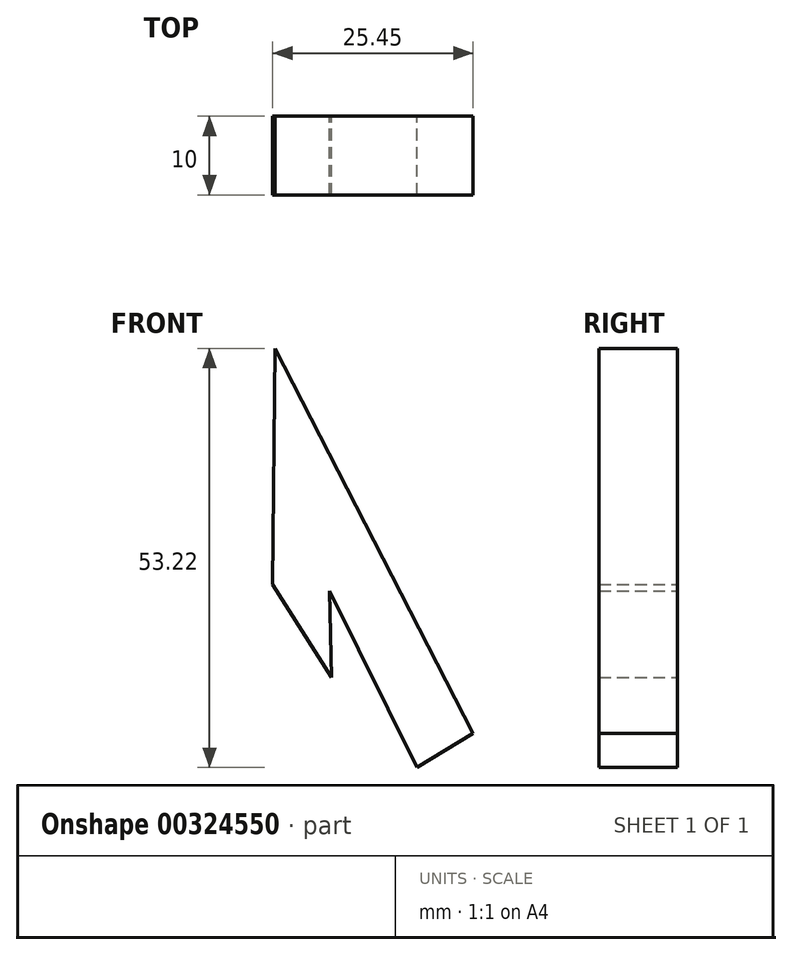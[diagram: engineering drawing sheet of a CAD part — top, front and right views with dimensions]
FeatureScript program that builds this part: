
annotation { "Feature Type Name" : "Feature", "Feature Type Description" : "" }
export const myFeature = defineFeature(function(context is Context, id is Id, definition is map)
    precondition{}
    {
        {
            var Q0;
            Q0=qCreatedBy(makeId("Front.planeOp"),FACE);
            var sketch = newSketch(context, id + "F0", { "sketchPlane" : qUnion([Q0])});
            skPoint(sketch, "E0", {"position": v(0, 0) * mm});
            skPoint(sketch, "E1", {"position": v(-25.12, 48.93) * mm});
            skLineSegment(sketch, "E2", {"start": v(-25.12, 48.93) * mm, "end": v(0, 0) * mm});
            skPoint(sketch, "E3", {"position": v(-25.45, 18.93) * mm});
            skLineSegment(sketch, "E4", {"start": v(-25.45, 18.93) * mm, "end": v(-25.12, 48.93) * mm});
            skPoint(sketch, "E5", {"position": v(-17.95, 7.1) * mm});
            skLineSegment(sketch, "E6", {"start": v(-17.95, 7.1) * mm, "end": v(-25.45, 18.93) * mm});
            skPoint(sketch, "E7", {"position": v(-18.21, 18.1) * mm});
            skLineSegment(sketch, "E8", {"start": v(-18.21, 18.1) * mm, "end": v(-17.95, 7.1) * mm});
            skPoint(sketch, "E9", {"position": v(-7.1, -4.3) * mm});
            skLineSegment(sketch, "E10", {"start": v(-7.1, -4.3) * mm, "end": v(-18.21, 18.1) * mm});
            skLineSegment(sketch, "E11", {"start": v(0, 0) * mm, "end": v(-7.1, -4.3) * mm});
            skSolve(sketch);
        }
        {
            var Q0;
            Q0=makeQuery(id+"F0.imprint","IMPRINT",FACE,{"disambiguationData":[TD([[makeQuery(id+"F0.imprint","IMPRINT",EDGE,{"derivedFrom":sQuery(id+"F0.wireOp",EDGE,"E2")}),-1.0]])]});
            extrude(context, id + "F1", {"entities" : qUnion([Q0]), "depth" : 10 * mm});
        }
    });
